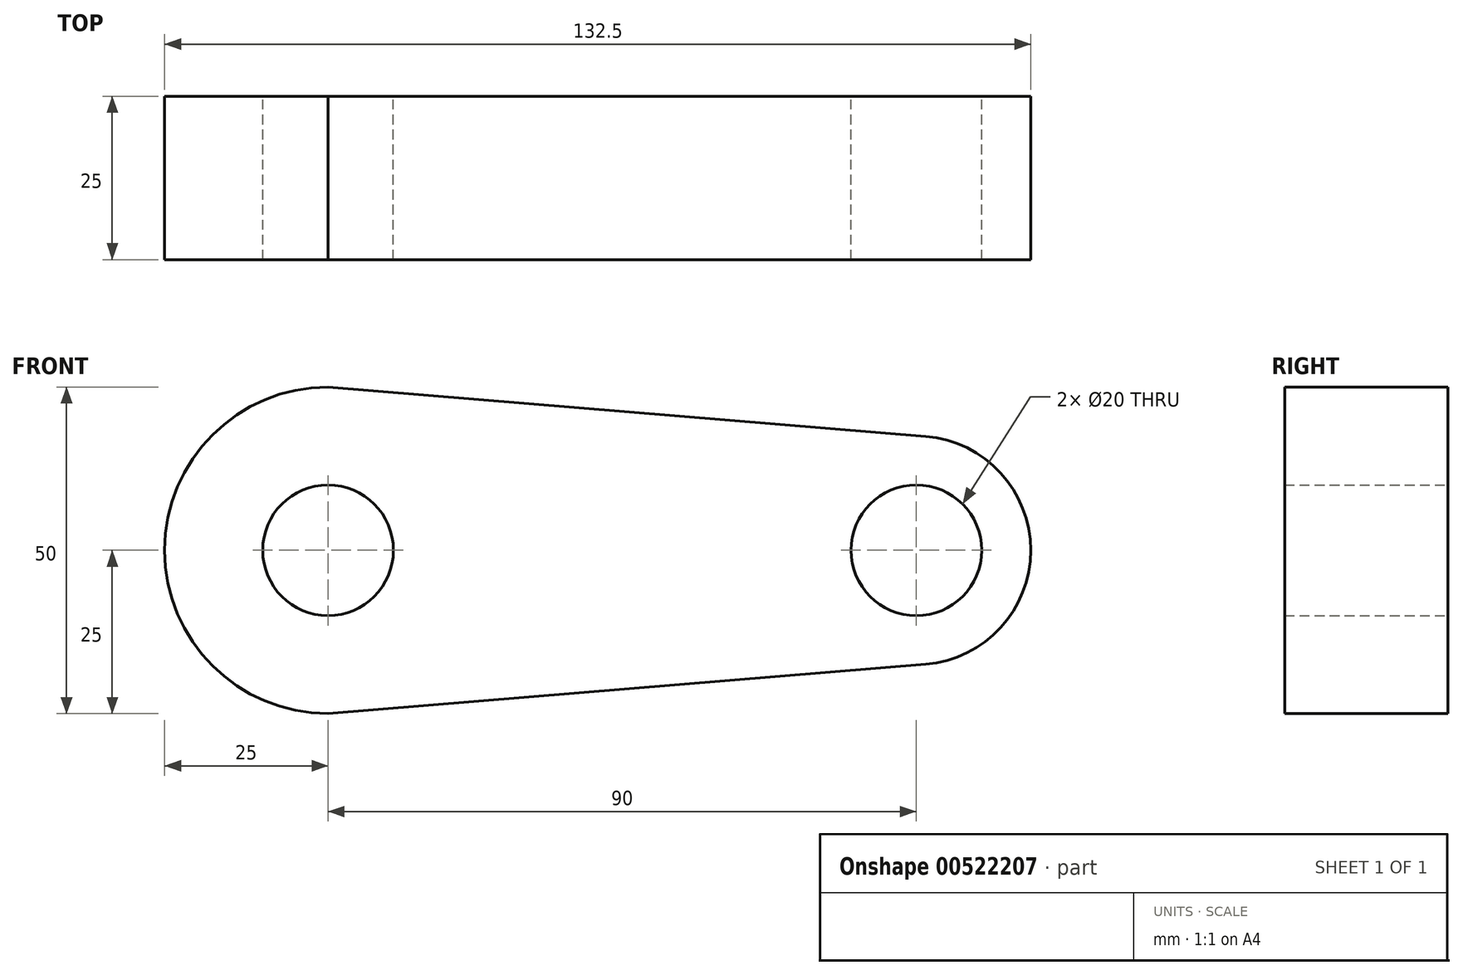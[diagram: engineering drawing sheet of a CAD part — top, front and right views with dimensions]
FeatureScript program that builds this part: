
annotation { "Feature Type Name" : "Feature", "Feature Type Description" : "" }
export const myFeature = defineFeature(function(context is Context, id is Id, definition is map)
    precondition{}
    {
        {
            var Q0;
            Q0=qCreatedBy(makeId("Front.planeOp"),FACE);
            var sketch = newSketch(context, id + "F0", { "sketchPlane" : qUnion([Q0])});
            skCircle(sketch, "E0", {"center": v(0, 0) * mm, "radius": 25 * mm});
            skCircle(sketch, "E1", {"center": v(90, 0) * mm, "radius": 17.5 * mm});
            skCircle(sketch, "E2", {"center": v(0, 0) * mm, "radius": 10 * mm});
            skCircle(sketch, "E3", {"center": v(90, 0) * mm, "radius": 10 * mm});
            skLineSegment(sketch, "E4", {"start": v(0, 25) * mm, "end": v(91.44, 17.44) * mm});
            skLineSegment(sketch, "E5", {"start": v(0, -25) * mm, "end": v(91.44, -17.44) * mm});
            skSolve(sketch);
        }
        {
            var Q0;
            Q0=makeQuery(id+"F0.imprint","IMPRINT",FACE,{"disambiguationData":[TD([[makeQuery(id+"F0.imprint","IMPRINT",EDGE,{"derivedFrom":sQuery(id+"F0.wireOp",EDGE,"E3")}),-1.0]])]});
            var Q1;
            Q1=makeQuery(id+"F0.imprint","IMPRINT",FACE,{"disambiguationData":[TD([[makeQuery(id+"F0.imprint","IMPRINT",EDGE,{"derivedFrom":sQuery(id+"F0.wireOp",EDGE,"E2")}),-1.0]])]});
            var Q2;
            {var subQ0=sQuery(id+"F0.wireOp",EDGE,"E4");var subQ1=sQuery(id+"F0.wireOp",EDGE,"E0");var subQ2=makeQuery(id+"F0.imprint","INTERSECT",VERTEX,{"disambiguationData":[OD(1.0)],"derivedFrom":[subQ1,subQ0]});Q2=makeQuery(id+"F0.imprint","IMPRINT",FACE,{"disambiguationData":[TD([[makeQuery(id+"F0.imprint","IMPRINT",EDGE,{"disambiguationData":[TD([[subQ2,1.0]])],"derivedFrom":subQ1}),-1.0]])]});}
            extrude(context, id + "F1", {"entities" : qUnion([Q0, Q1, Q2]), "depth" : 25 * mm, "offsetDistance" : 25 * mm});
        }
    });
